# Revit family: NBS_DudleyIndustries_TltPprBulkDpnsrs_PlatinumRange_ToiletPaperDispenser
name_source: partatom
category: Specialty Equipment
revit_build: Autodesk Revit 2016 (Build: 20150220_1215(x64)
units: mm (PartAtom-declared; Revit-internal decimal feet)

## family parameters
Cut with Voids When Loaded = No
Host = Face
OmniClass Number = 23.40.20.21.21
OmniClass Title = Toilet Paper Dispensers
Part Type = Normal
Room Calculation Point = No
Round Connector Dimension = Use Diameter
Shared = No

## types (1)
- PlatinumRangeToiletPaperDispenser
    AssetType = Fixed
    BIMObjectName = NBS_DudleyIndustries_ToiletPaperBulkDispensers_Platinumrange_ToiletPaperDispenser
    Category = Pr_40_70_22_90:Toilet paper dispensers
    Color = Stainless steel
    Default Elevation = 1200 mm
    Description = 2 roll toilet paper dispenser
    DispenserCaseMaterial = NBS_Concept
    DispenserLockMaterial = NBS_Concept
    DurationUnit = year
    ExpectedLife = 5
    Finish = Brushed/Lacquered (77019CB)
    Form = Wall mounted
    IfcExportAs = IfcFurnitureType
    IfcExportType = NOTDEFINED
    MainColor = Stainless Steel
    ManufacturerName = Dudley Industries
    ManufacturerURL = www.dudleyindustries.com/
    Material = Stainless Steel
    MaterialsBody = Stainless Steel
    MaterialsFinishColour = Brushed/Lacquered (77019CB)
    ModelNumber = 77019
    ModelReference = Platinum range: Toilet Paper Dispenser
    NBSCertification = www.nationalbimlibrary.com/cert/yeyya5fs
    NBSDescription = Toilet paper bulk dispensers
    NBSReference = 45-35-72/366
    Name = ToiletPaperBulkDispensers_PlatinumRange_ToiletPaperDispenser_DudleyIndustries
    NominalDepth = 172 mm  [stored 0.564304 ft]
    NominalHeight = 280 mm
    NominalLength = 162 mm  [stored 0.531496 ft]
    NominalWidth = 162 mm  [stored 0.531496 ft]
    Operation = Pull out
    ProductInformation = www.dudleyindustries.com/wp-content/uploads/2016/11/2-Roll-Toilet-Paper-Dispenser-1.pdf
    Size = 162 x 280 x 172 mm
    Uniclass2015Code = Pr_40_70_22_90
    Uniclass2015Title = Toilet paper dispensers
    Uniclass2015Version = Products v1.7
    Version = 2
    WarrantyDescription = 1 year warranty
    WarrantyDurationParts = 1
    WarrantyDurationUnit = year

note: [stored X ft] marks values corroborated as IEEE doubles in the binary element streams (Revit-internal decimal feet)

## geometry (parser evidence)
native form markers: Sweep x2
no freeform markers — native parametric forms only
